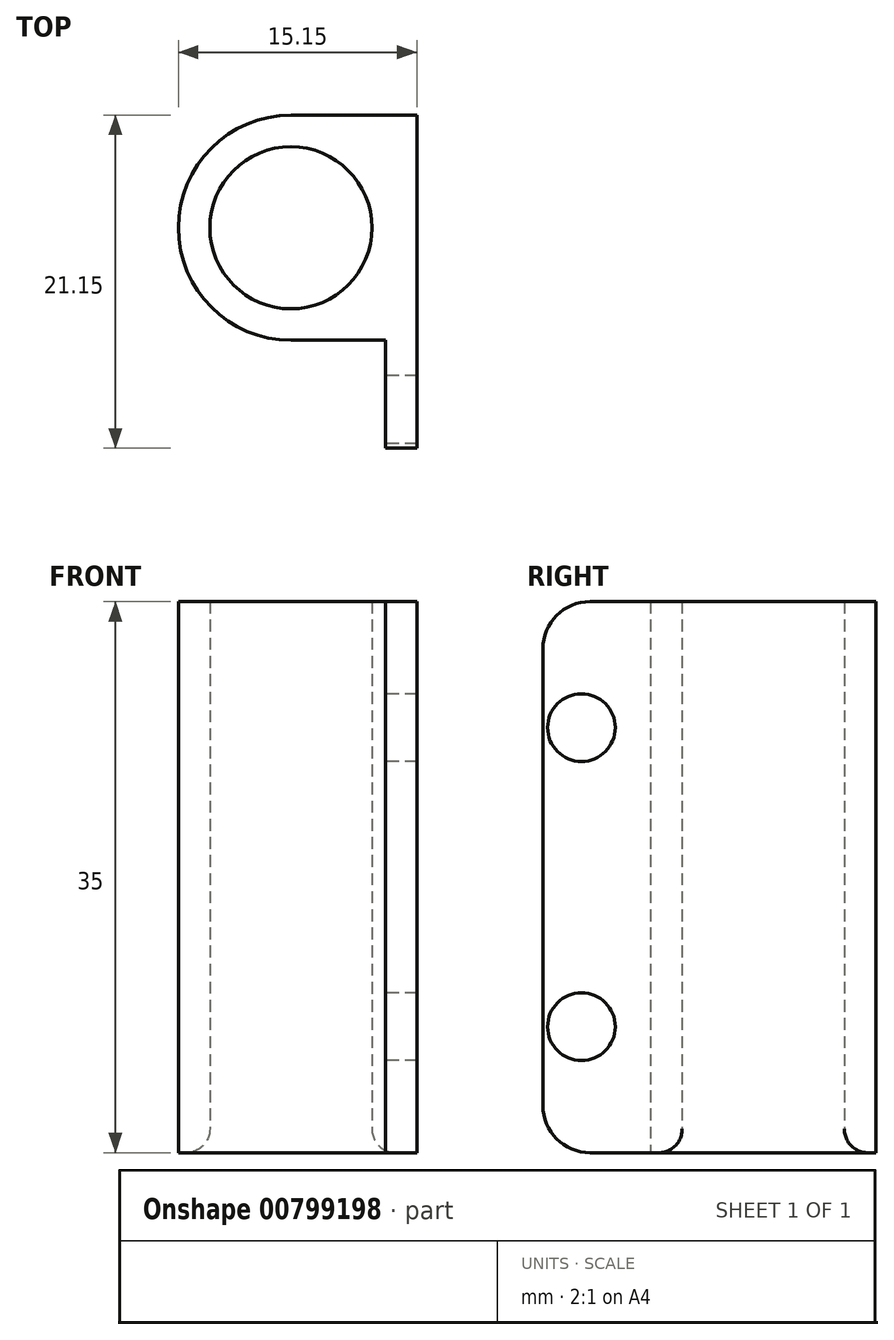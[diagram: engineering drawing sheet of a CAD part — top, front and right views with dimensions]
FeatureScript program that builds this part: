
annotation { "Feature Type Name" : "Feature", "Feature Type Description" : "" }
export const myFeature = defineFeature(function(context is Context, id is Id, definition is map)
    precondition{}
    {
        {
            var Q0;
            Q0=qCreatedBy(makeId("Top.planeOp"),FACE);
            var sketch = newSketch(context, id + "F0", { "sketchPlane" : qUnion([Q0])});
            skCircle(sketch, "E0", {"center": v(0, 0) * mm, "radius": 5.15 * mm});
            skCircle(sketch, "E1.0", {"center": v(0, 0) * mm, "radius": 7.15 * mm});
            skLineSegment(sketch, "E2", {"start": v(0, 0) * mm, "end": v(8, 0) * mm});
            skLineSegment(sketch, "E3", {"start": v(8, 0) * mm, "end": v(8, 7.15) * mm});
            skLineSegment(sketch, "E4", {"start": v(0, 7.15) * mm, "end": v(8, 7.15) * mm});
            skLineSegment(sketch, "E5", {"start": v(8, 0) * mm, "end": v(8, -14) * mm});
            skLineSegment(sketch, "E6", {"start": v(8, -14) * mm, "end": v(6, -14) * mm});
            skLineSegment(sketch, "E7", {"start": v(0, -7.15) * mm, "end": v(6, -7.15) * mm});
            skLineSegment(sketch, "E8", {"start": v(6, -7.15) * mm, "end": v(6, -14) * mm});
            skSolve(sketch);
        }
        {
            var Q0;
            Q0=makeQuery(id+"F0.imprint","IMPRINT",FACE,{"disambiguationData":[TD([[makeQuery(id+"F0.imprint","IMPRINT",EDGE,{"derivedFrom":sQuery(id+"F0.wireOp",EDGE,"E0")}),-1.0]])]});
            var Q1;
            {var subQ0=sQuery(id+"F0.wireOp",EDGE,"E5");Q1=makeQuery(id+"F0.imprint","IMPRINT",FACE,{"disambiguationData":[TD([[makeQuery(id+"F0.imprint","IMPRINT",EDGE,{"derivedFrom":subQ0}),-1.0]])]});}
            var Q2;
            {var subQ0=sQuery(id+"F0.wireOp",EDGE,"E3");Q2=makeQuery(id+"F0.imprint","IMPRINT",FACE,{"disambiguationData":[TD([[makeQuery(id+"F0.imprint","IMPRINT",EDGE,{"derivedFrom":subQ0}),1.0]])]});}
            extrude(context, id + "F1", {"entities" : qUnion([Q0, Q1, Q2]), "depth" : 35 * mm, "offsetDistance" : 25 * mm});
        }
        {
            var Q0;
            Q0=makeQuery(id+"F1.opExtrude","SWEPT_FACE",FACE,{"disambiguationData":[OSD([sQuery(id+"F0.wireOp",EDGE,"E8")])]});
            var sketch = newSketch(context, id + "F2", { "sketchPlane" : qUnion([Q0])});
            skCircle(sketch, "E9", {"center": v(11.55, 8) * mm, "radius": 2.15 * mm});
            skCircle(sketch, "E10", {"center": v(11.55, 27) * mm, "radius": 2.15 * mm});
            skSolve(sketch);
        }
        {
            var Q0;
            Q0=sQuery(id+"F2.wireOp",VERTEX,"E9.center");
            var Q1;
            Q1=sQuery(id+"F2.wireOp",VERTEX,"E10.center");
            var Q2;
            Q2=makeQuery(id+"F1.opExtrude","SWEPT_BODY",BODY,{"disambiguationData":[OSD([sQuery(id+"F0.wireOp",EDGE,"E0"),sQuery(id+"F0.wireOp",EDGE,"E1.0"),sQuery(id+"F0.wireOp",EDGE,"E3"),sQuery(id+"F0.wireOp",EDGE,"J3KKdDFu-yuE8-6Pt3-skXl-feLDG5kr8hMT"),sQuery(id+"F0.wireOp",EDGE,"E4"),sQuery(id+"F0.wireOp",EDGE,"j2dA3E7N-Xl26-7CnG-Wyk1-8kZz27HhTYN5"),sQuery(id+"F0.wireOp",EDGE,"E5"),sQuery(id+"F0.wireOp",EDGE,"E6"),sQuery(id+"F0.wireOp",EDGE,"E7"),sQuery(id+"F0.wireOp",EDGE,"E8")])]});
            hole(context, id + "F3", {"style" : HoleStyle.SIMPLE, "endStyle" : HoleEndStyle.THROUGH, "holeDiameter" : 4.3 * mm, "majorDiameter" : 5 * mm, "isTappedThrough" : true, "tappedDepth" : 12 * mm, "tapClearance" : 3, "locations" : qUnion([Q0, Q1]), "scope" : qUnion([Q2])});
        }
        {
            var Q0;
            Q0=makeQuery(id+"F1.opExtrude","CAP_EDGE",EDGE,{"disambiguationData":[OSD([sQuery(id+"F0.wireOp",EDGE,"E6")])],"isStart":true});
            var Q1;
            Q1=makeQuery(id+"F1.opExtrude","CAP_EDGE",EDGE,{"disambiguationData":[OSD([sQuery(id+"F0.wireOp",EDGE,"E6")])],"isStart":false});
            fillet(context, id + "F4", {"entities" : qUnion([Q0, Q1]), "radius" : 3 * mm, "tangentPropagation" : true, "allowEdgeOverflow" : false});
        }
        {
            var Q0;
            Q0=makeQuery(id+"F1.opExtrude","CAP_EDGE",EDGE,{"disambiguationData":[OSD([sQuery(id+"F0.wireOp",EDGE,"E0")])],"isStart":true});
            fillet(context, id + "F5", {"entities" : qUnion([Q0]), "radius" : 1.5 * mm, "tangentPropagation" : true, "allowEdgeOverflow" : false});
        }
    });
